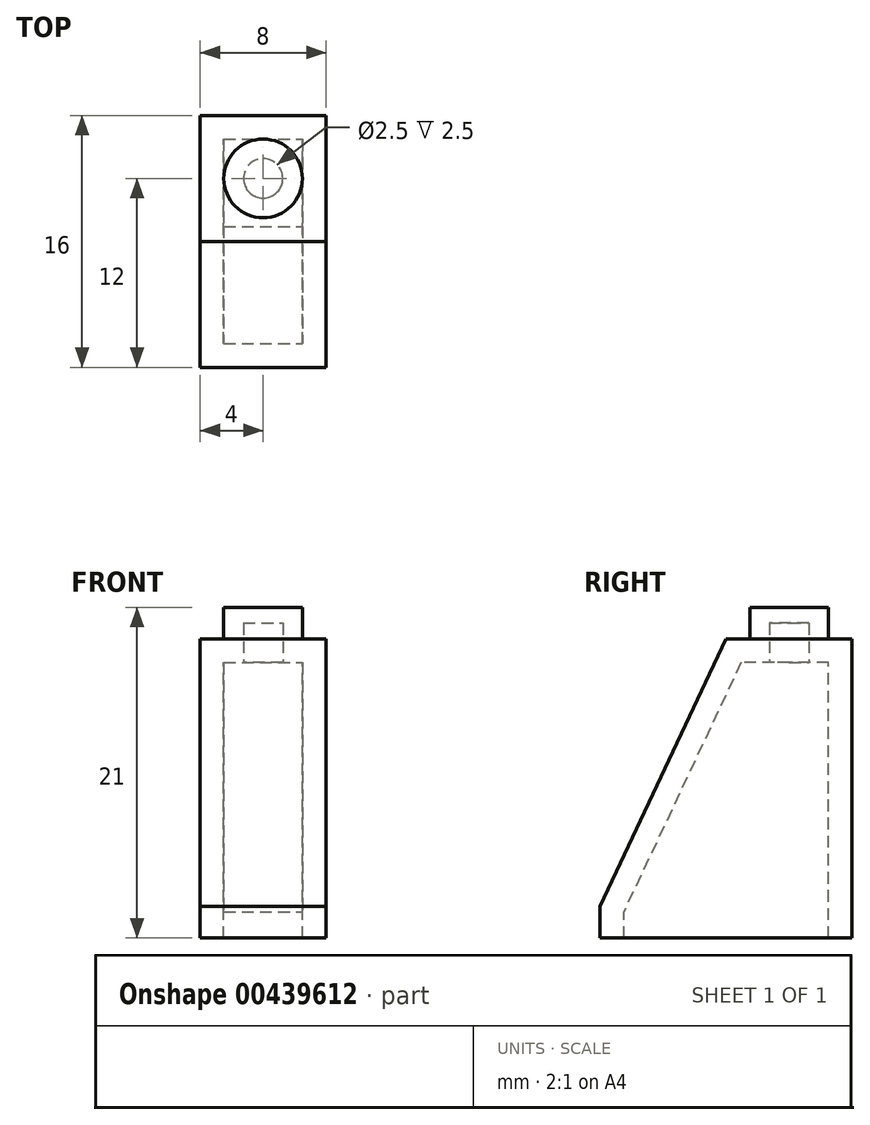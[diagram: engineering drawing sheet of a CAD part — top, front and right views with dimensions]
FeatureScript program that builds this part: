
annotation { "Feature Type Name" : "Feature", "Feature Type Description" : "" }
export const myFeature = defineFeature(function(context is Context, id is Id, definition is map)
    precondition{}
    {
        {
            var Q0;
            Q0=qCreatedBy(makeId("Right.planeOp"),FACE);
            var sketch = newSketch(context, id + "F0", { "sketchPlane" : qUnion([Q0])});
            skLineSegment(sketch, "E0.bottom", {"start": v(0, 0) * mm, "end": v(16, 0) * mm});
            skLineSegment(sketch, "E0.top", {"start": v(8, 19) * mm, "end": v(16, 19) * mm});
            skLineSegment(sketch, "E0.left", {"start": v(0, 0) * mm, "end": v(0, 2) * mm});
            skLineSegment(sketch, "E0.right", {"start": v(16, 0) * mm, "end": v(16, 19) * mm});
            skLineSegment(sketch, "E1", {"start": v(8, 19) * mm, "end": v(0, 2) * mm});
            skSolve(sketch);
        }
        {
            var Q0;
            Q0 = qSketchRegion(id + "F0", true);
            extrude(context, id + "F1", {"entities" : qUnion([Q0]), "depth" : 4 * mm});
        }
        {
            var Q0;
            Q0=makeQuery(id+"F1.opExtrude","CAP_FACE",FACE,{"disambiguationData":[OSD([sQuery(id+"F0.wireOp",EDGE,"E0.bottom"),sQuery(id+"F0.wireOp",EDGE,"E0.top"),sQuery(id+"F0.wireOp",EDGE,"E0.left"),sQuery(id+"F0.wireOp",EDGE,"E0.right"),sQuery(id+"F0.wireOp",EDGE,"E1")])],"isStart":false});
            var sketch = newSketch(context, id + "F2", { "sketchPlane" : qUnion([Q0])});
            skLineSegment(sketch, "E2.0", {"start": v(14.5, 17.5) * mm, "end": v(8.95, 17.5) * mm});
            skLineSegment(sketch, "E2.1", {"start": v(14.5, 0) * mm, "end": v(14.5, 17.5) * mm});
            skLineSegment(sketch, "E2.3", {"start": v(8.95, 17.5) * mm, "end": v(1.5, 1.66) * mm});
            skLineSegment(sketch, "E3.0", {"start": v(1.5, 0) * mm, "end": v(1.5, 1.66) * mm});
            skLineSegment(sketch, "E4", {"start": v(1.5, 0) * mm, "end": v(14.5, 0) * mm});
            skSolve(sketch);
        }
        {
            var Q0;
            Q0=makeQuery(id+"F2.imprint","IMPRINT",FACE,{"disambiguationData":[TD([[makeQuery(id+"F2.imprint","IMPRINT",EDGE,{"derivedFrom":sQuery(id+"F2.wireOp",EDGE,"E2.0")}),1.0]])]});
            extrude(context, id + "F3", {"entities" : qUnion([Q0]), "operationType" : NewBodyOperationType.REMOVE, "oppositeDirection" : true, "depth" : 2.5 * mm});
        }
        {
            var Q0;
            Q0=makeQuery(id+"F1.opExtrude","SWEPT_BODY",BODY,{"disambiguationData":[OSD([sQuery(id+"F0.wireOp",EDGE,"E0.bottom"),sQuery(id+"F0.wireOp",EDGE,"E0.top"),sQuery(id+"F0.wireOp",EDGE,"E0.left"),sQuery(id+"F0.wireOp",EDGE,"E0.right"),sQuery(id+"F0.wireOp",EDGE,"E1")])]});
            var Q1;
            Q1=makeQuery(id+"F1.opExtrude","CAP_FACE",FACE,{"disambiguationData":[OSD([sQuery(id+"F0.wireOp",EDGE,"E0.bottom"),sQuery(id+"F0.wireOp",EDGE,"E0.top"),sQuery(id+"F0.wireOp",EDGE,"E0.left"),sQuery(id+"F0.wireOp",EDGE,"E0.right"),sQuery(id+"F0.wireOp",EDGE,"E1")])],"isStart":false});
            mirror(context, id + "F4", {"operationType" : NewBodyOperationType.ADD, "entities" : qUnion([Q0]), "mirrorPlane" : qUnion([Q1])});
        }
        {
            var Q0;
            Q0=makeQuery(id+"F1.opExtrude","SWEPT_FACE",FACE,{"disambiguationData":[OSD([sQuery(id+"F0.wireOp",EDGE,"E0.top")])]});
            var sketch = newSketch(context, id + "F5", { "sketchPlane" : qUnion([Q0])});
            skCircle(sketch, "E5", {"center": v(4, 12) * mm, "radius": 2.5 * mm});
            skSolve(sketch);
        }
        {
            var Q0;
            Q0=makeQuery(id+"F5.imprint","IMPRINT",FACE,{"disambiguationData":[TD([[makeQuery(id+"F5.imprint","IMPRINT",EDGE,{"derivedFrom":sQuery(id+"F5.wireOp",EDGE,"E5")}),1.0]])]});
            extrude(context, id + "F6", {"entities" : qUnion([Q0]), "operationType" : NewBodyOperationType.ADD, "depth" : 2 * mm});
        }
        {
            var Q0;
            Q0=makeQuery(id+"F1.opExtrude","SWEPT_FACE",FACE,{"disambiguationData":[OSD([sQuery(id+"F0.wireOp",EDGE,"E0.bottom")])]});
            var sketch = newSketch(context, id + "F7", { "sketchPlane" : qUnion([Q0])});
            skCircle(sketch, "E6", {"center": v(4, -12) * mm, "radius": 1.25 * mm});
            skSolve(sketch);
        }
        {
            var Q0;
            Q0 = qSketchRegion(id + "F7", true);
            extrude(context, id + "F8", {"entities" : qUnion([Q0]), "operationType" : NewBodyOperationType.REMOVE, "oppositeDirection" : true, "depth" : 20 * mm});
        }
    });
